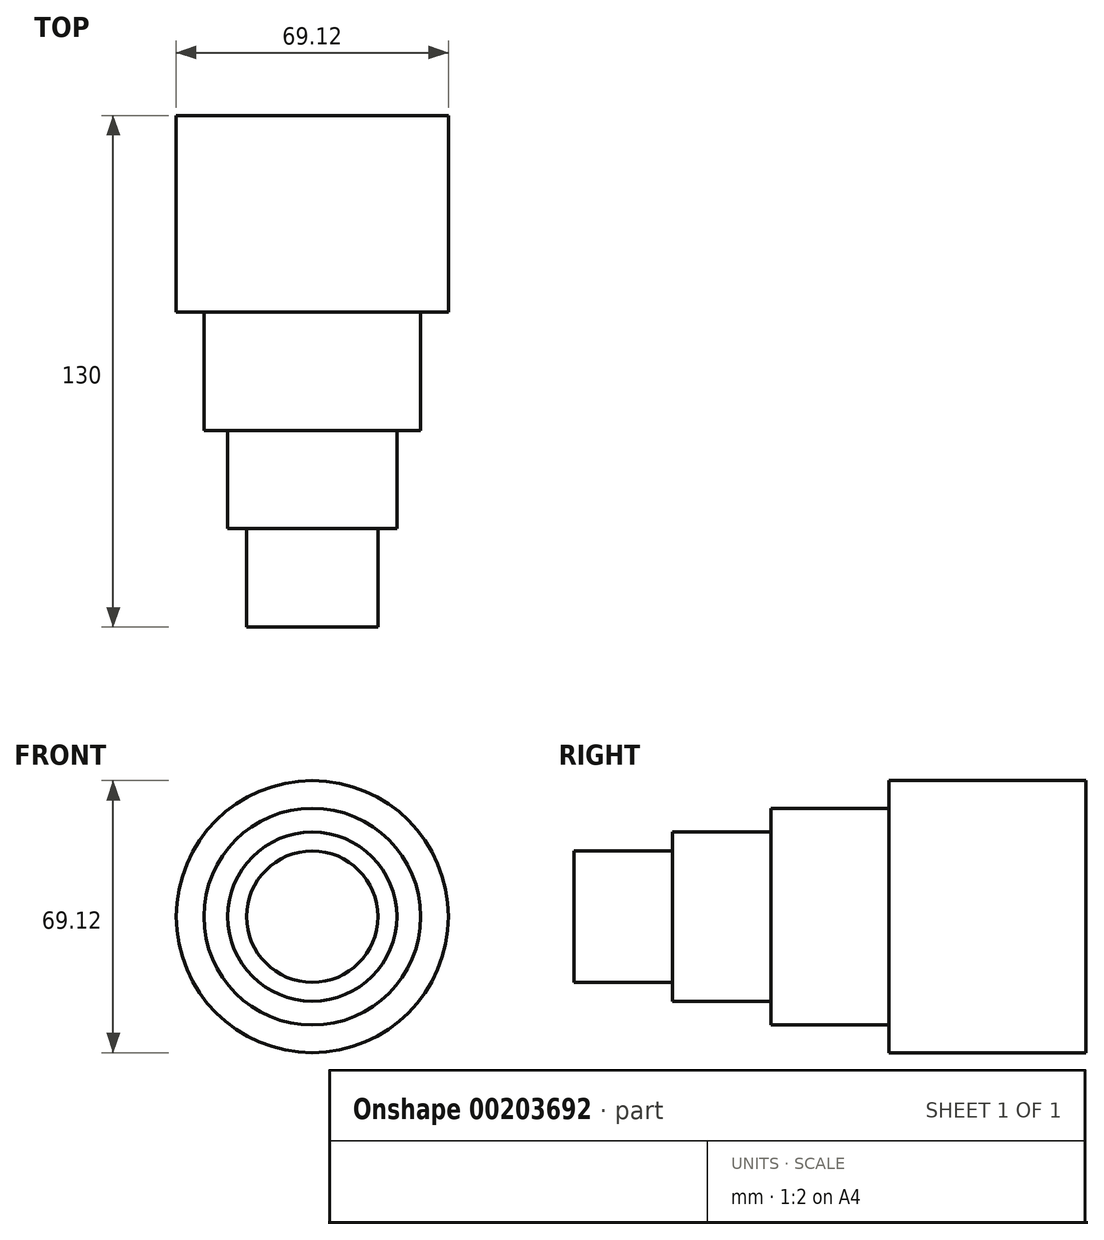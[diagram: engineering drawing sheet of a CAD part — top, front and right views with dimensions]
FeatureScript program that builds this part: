
annotation { "Feature Type Name" : "Feature", "Feature Type Description" : "" }
export const myFeature = defineFeature(function(context is Context, id is Id, definition is map)
    precondition{}
    {
        {
            var Q0;
            Q0=qCreatedBy(makeId("Front.planeOp"),FACE);
            var sketch = newSketch(context, id + "F0", { "sketchPlane" : qUnion([Q0])});
            skCircle(sketch, "E0", {"center": v(0, 0) * mm, "radius": 34.56 * mm});
            skSolve(sketch);
        }
        {
            var Q0;
            Q0=makeQuery(id+"F0.imprint","IMPRINT",FACE,{"disambiguationData":[TD([[makeQuery(id+"F0.imprint","IMPRINT",EDGE,{"derivedFrom":sQuery(id+"F0.wireOp",EDGE,"E0")}),1.0]])]});
            extrude(context, id + "F1", {"entities" : qUnion([Q0]), "depth" : 50 * mm});
        }
        {
            var Q0;
            Q0=makeQuery(id+"F1.opExtrude","CAP_FACE",FACE,{"disambiguationData":[OSD([sQuery(id+"F0.wireOp",EDGE,"E0")])],"isStart":false});
            var sketch = newSketch(context, id + "F2", { "sketchPlane" : qUnion([Q0])});
            skCircle(sketch, "E1", {"center": v(0, 0) * mm, "radius": 27.54 * mm});
            skSolve(sketch);
        }
        {
            var Q0;
            Q0 = qSketchRegion(id + "F2", true);
            extrude(context, id + "F3", {"entities" : qUnion([Q0]), "operationType" : NewBodyOperationType.ADD, "depth" : 30 * mm});
        }
        {
            var Q0;
            Q0=makeQuery(id+"F3.opExtrude","CAP_FACE",FACE,{"disambiguationData":[OSD([sQuery(id+"F2.wireOp",EDGE,"E1")])],"isStart":false});
            var sketch = newSketch(context, id + "F4", { "sketchPlane" : qUnion([Q0])});
            skCircle(sketch, "E2", {"center": v(0, 0) * mm, "radius": 21.5 * mm});
            skSolve(sketch);
        }
        {
            var Q0;
            Q0 = qSketchRegion(id + "F4", true);
            extrude(context, id + "F5", {"entities" : qUnion([Q0]), "operationType" : NewBodyOperationType.ADD, "depth" : 25 * mm});
        }
        {
            var Q0;
            Q0=makeQuery(id+"F5.opExtrude","CAP_FACE",FACE,{"disambiguationData":[OSD([sQuery(id+"F4.wireOp",EDGE,"E2")])],"isStart":false});
            var sketch = newSketch(context, id + "F6", { "sketchPlane" : qUnion([Q0])});
            skCircle(sketch, "E3", {"center": v(0, 0) * mm, "radius": 16.68 * mm});
            skSolve(sketch);
        }
        {
            var Q0;
            Q0 = qSketchRegion(id + "F6", true);
            extrude(context, id + "F7", {"entities" : qUnion([Q0]), "operationType" : NewBodyOperationType.ADD, "depth" : 25 * mm});
        }
    });
